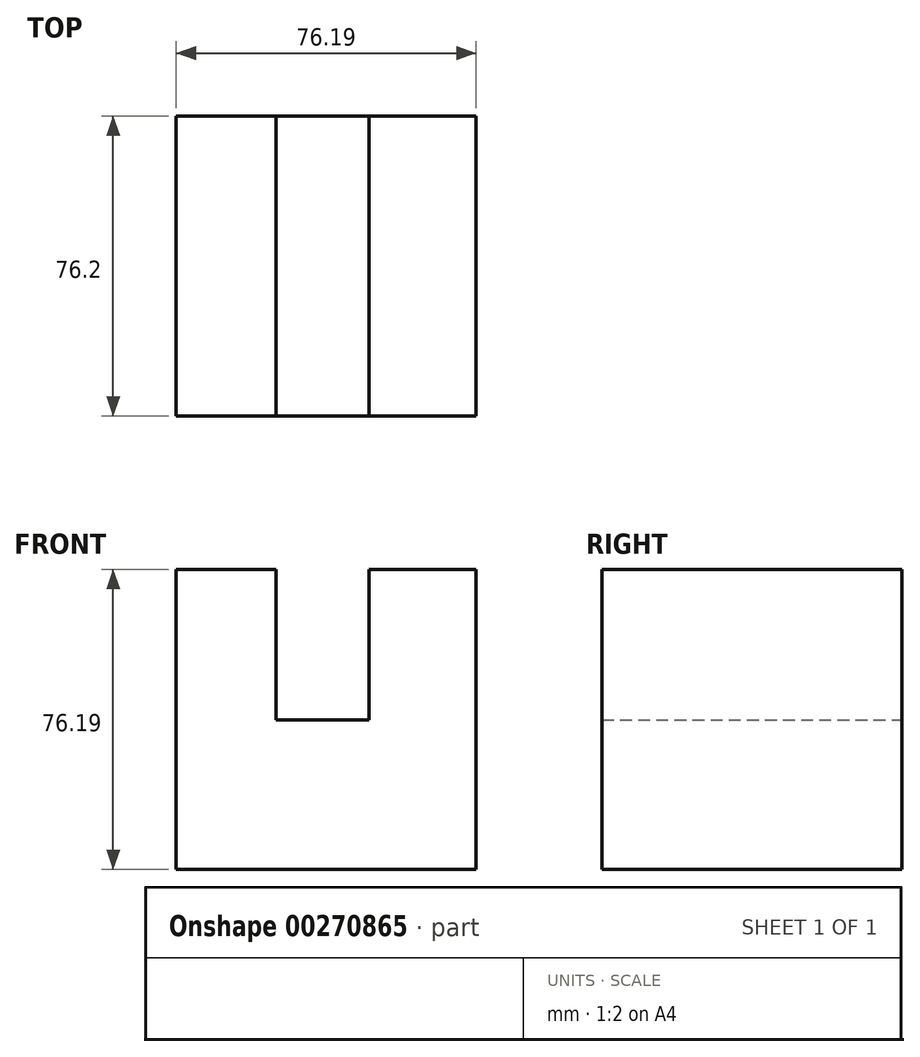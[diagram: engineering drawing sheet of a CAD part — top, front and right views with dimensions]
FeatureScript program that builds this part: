
annotation { "Feature Type Name" : "Feature", "Feature Type Description" : "" }
export const myFeature = defineFeature(function(context is Context, id is Id, definition is map)
    precondition{}
    {
        {
            var Q0;
            Q0=qCreatedBy(makeId("Front.planeOp"),FACE);
            var sketch = newSketch(context, id + "F0", { "sketchPlane" : qUnion([Q0])});
            skLineSegment(sketch, "E0", {"start": v(0, 0) * mm, "end": v(-76.2, 0) * mm});
            skLineSegment(sketch, "E1", {"start": v(-76.2, 0) * mm, "end": v(-76.2, 76.2) * mm});
            skLineSegment(sketch, "E2", {"start": v(-76.2, 76.2) * mm, "end": v(-50.8, 76.2) * mm});
            skLineSegment(sketch, "E3", {"start": v(-50.8, 76.2) * mm, "end": v(-50.8, 37.97) * mm});
            skLineSegment(sketch, "E4", {"start": v(-50.8, 37.97) * mm, "end": v(-27.23, 37.97) * mm});
            skLineSegment(sketch, "E5", {"start": v(-27.23, 37.97) * mm, "end": v(-27.23, 76.2) * mm});
            skLineSegment(sketch, "E6", {"start": v(-27.23, 76.2) * mm, "end": v(0, 76.2) * mm});
            skLineSegment(sketch, "E7", {"start": v(0, 76.2) * mm, "end": v(0, 0) * mm});
            skSolve(sketch);
        }
        {
            var Q0;
            Q0 = qSketchRegion(id + "F0", true);
            extrude(context, id + "F1", {"entities" : qUnion([Q0]), "depth" : 76.2 * mm});
        }
    });
